# Revit family: Storage-Mounted-Teknion-BRHL_Tower_with_Full _Solid_Door_High_Secondary_Desk-R2019
name_source: partatom
category: Furniture
units: mm (PartAtom-declared; Revit-internal decimal feet)

## family parameters
Always vertical = Yes
Cut with Voids When Loaded = No
OmniClass Number = 23.40.70.14.64.21
OmniClass Title = Systems Furniture
Room Calculation Point = No
Shared = Yes
Work Plane-Based = No

## types (2) — shared parameters
Assembly Code = E2020200
Depth = 18 "
Manufacturer = Teknion
Manufacturer Fax = 416.661.4586
Part Number = BRHL
Product Documentation Link = http://www.teknion.com
Product Line = Expansion Casegoods
Product Page URL = https://www.teknion.com
Series = Expansion Casegoods
Sustainability Data = http://www.teknion.com
URL = http://www.teknion.com
Unit Weight URL = http://www.teknion.com
Warranty = https://www.teknion.com
Width = 17.91 "

## per-type parameters (varying)
| type | Description | Height | Model |
| 18" x 18" x 66" | Tower with Full Solid Door - High Secondary Desk Mounted, Shelf Interior Configuration, 18" Depth, 18" Width, 66" Height | 65.374 " | BRHLS181866_ |
| 18" x 18" x 72" | Tower with Full Solid Door - High Secondary Desk Mounted, Shelf Interior Configuration, 18" Depth, 18" Width, 72" Height | 71.626 " | BRHLS181872_ |

## geometry (parser evidence)
native form markers: Sweep x3
no freeform markers — native parametric forms only
